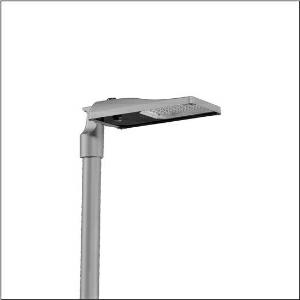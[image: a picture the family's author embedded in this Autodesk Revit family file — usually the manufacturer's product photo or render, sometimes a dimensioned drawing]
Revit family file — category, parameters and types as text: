
# Revit family: streetlight_sl_31_mini___st1_0a_5xh2d71t08ga_b82e
name_source: partatom
category: Lighting Fixtures
units: mm (PartAtom-declared; Revit-internal decimal feet)

## family parameters
Cut with Voids When Loaded = No
Host = Face
Light Source = No
Part Type = Normal
Room Calculation Point = No
Round Connector Dimension = Use Diameter
Shared = No

## types (1)
- --- (1 x LED, 4760 lm, 39.3 W, 2200K)
    Apparent Load = 39 VA
    CIE Flux Codes = 37 72 97 100 100
    Color Rendering = 70
    Color Temperature = 2200K
    Default Elevation = 1800 mm
    Description = Streetlight SL 31 mini D4i, Desk-Remote mast luminaire for post-top, side-entry; light control with lens of PMMA; light distribution: ST1.0a, direct asymmetric distribution, for standard-compliant lighting for roads and squares; LED: luminous flux: 4.760lm, light colour: 722, colour temperature: 2200K; luminous efficacy: 121,1lm/W; control: pre-setting: logarithmic dimming characteristic, flexible luminous flux parameterisation, time-dependent luminous flux control, constant luminous flux control, power reduction, intelligent temperature release in ECG and LED module, overheat protection; luminaire housing, of diecast aluminium, SITECO metallic grey (DB 702S), corrosivity category C5 high according to DIN EN ISO 12944; cover of toughened safety glass, transparent, mast flange of diecast aluminium, SITECO metallic grey (DB 702S), spigot size: 76/60mm, mast flange included unmounted; cable length: 6,5m, connection cable pre-assembled; mains connection: 220..240V, AC, 50/60Hz; power consumption (at start of service life): 39,3W / (at end of service life): 40,7W / (with reduced operation 50%): 18,1W; protection rating (complete): IP66; insulation class (complete): insulation class II (safety insulation); impact resistance: IK09; certification: CE, ENEC, ENEC+, VDE, UKCA, ZD4i; permissible operating ambient temperature for outdoor applications: -40..+50°C; packaging unit: 1 piece

Light Distribution: ST1.0a
    Height = 76 mm
    Lamp = 1 x LED
    Lamp Light Flux = 4760 lm
    Lamp Power = 39.3 W
    Lamp count = 1
    Length = 547 mm
    Luminous efficacy = 121 lm/W
    Manufacturer = Siteco
    ModVariant = No
    Model = 5XH2D71T08GA
    Number of Poles = 1
    OnlyDefault = Yes
    Power Factor = 1
    Product Name = Streetlight SL 31 mini | ST1.0a
    Product group = mast luminaire | pylon top
    ProductGroupID = 6100
    Protection Class = Protection class II
    Protection Degree = IP 66
    RLX_Detail_Level = 1
    RLX_Emergency_Light_Flux = 0 lm
    RLX_Emergency_Type = 0
    RLX_Emergency_Type_DB = No
    RlxData = <blob elided: 39693 chars, md5=5afb2f2b>
    Socket = socket
    Standby Power = 0 W
    System Light Flux = 4760 lm
    System Power = 39 W
    Type Comments = factory setting: luminous flux: 100 % | dim-lin: 254 | 798 mA
    Type Image = l_1300332.jpg
    URL = http://relux.com
    VarID = @adj_009397
    Voltage = 0 V
    Weight = 0.00 kg
    Width = 265 mm

## geometry (parser evidence)
native form markers: Blend x4, Sweep x9
no freeform markers — native parametric forms only
